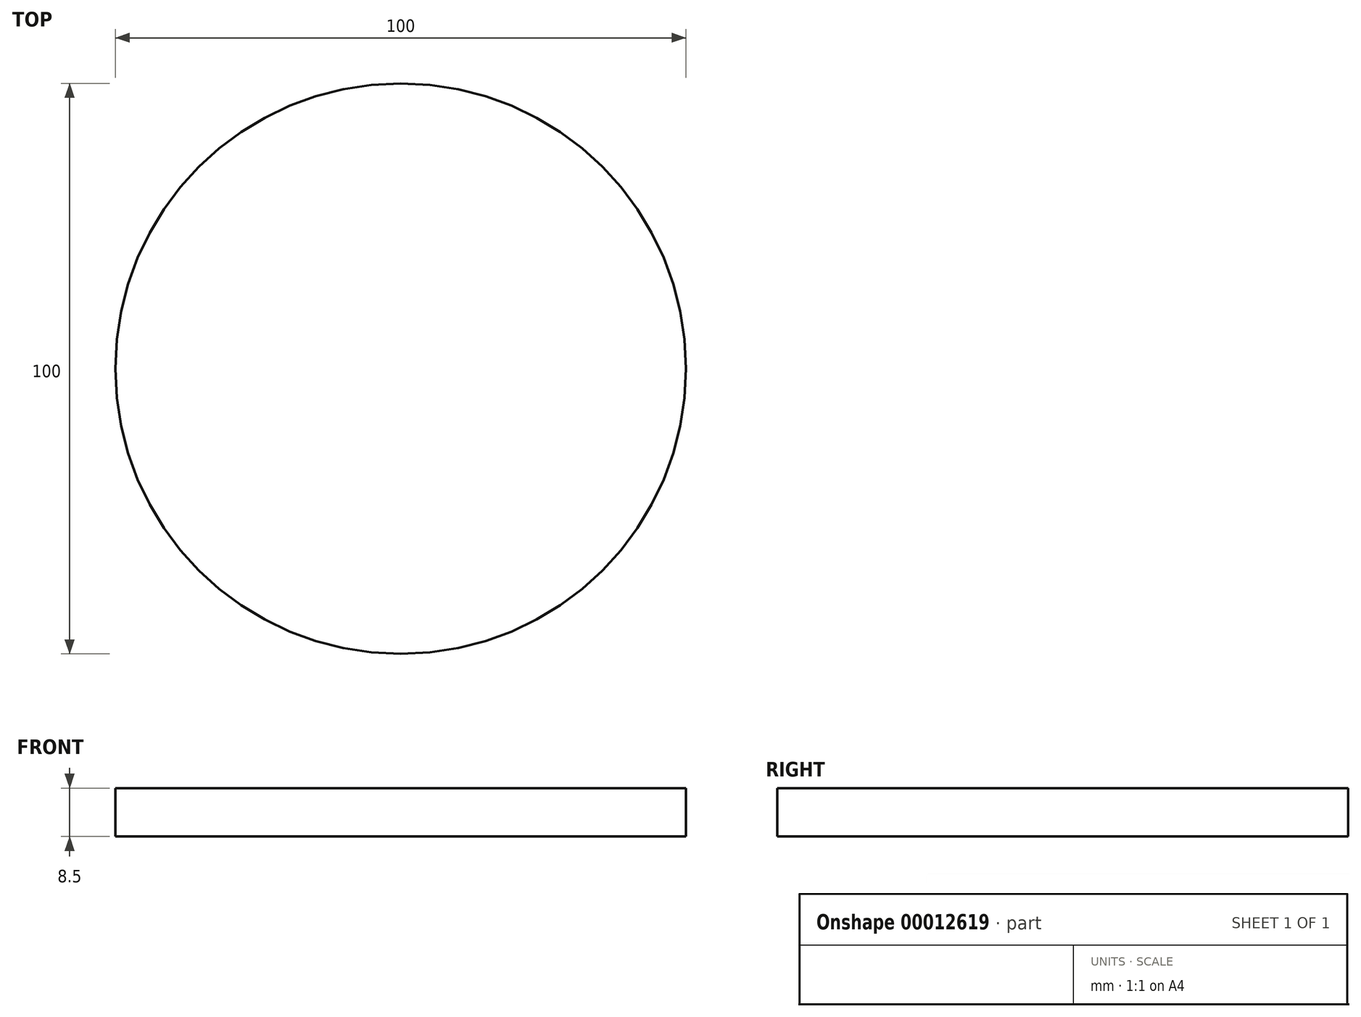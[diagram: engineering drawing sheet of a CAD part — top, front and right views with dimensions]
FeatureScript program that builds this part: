
annotation { "Feature Type Name" : "Feature", "Feature Type Description" : "" }
export const myFeature = defineFeature(function(context is Context, id is Id, definition is map)
    precondition{}
    {
        {
            var Q0;
            Q0=qCreatedBy(makeId("Top.planeOp"),FACE);
            var sketch = newSketch(context, id + "F0", { "sketchPlane" : qUnion([Q0])});
            skCircle(sketch, "E0", {"center": v(0, 0) * mm, "radius": 50 * mm});
            skSolve(sketch);
        }
        {
            var Q0;
            Q0 = qSketchRegion(id + "F0", true);
            extrude(context, id + "F1", {"entities" : qUnion([Q0]), "depth" : 8.5 * mm});
        }
    });
